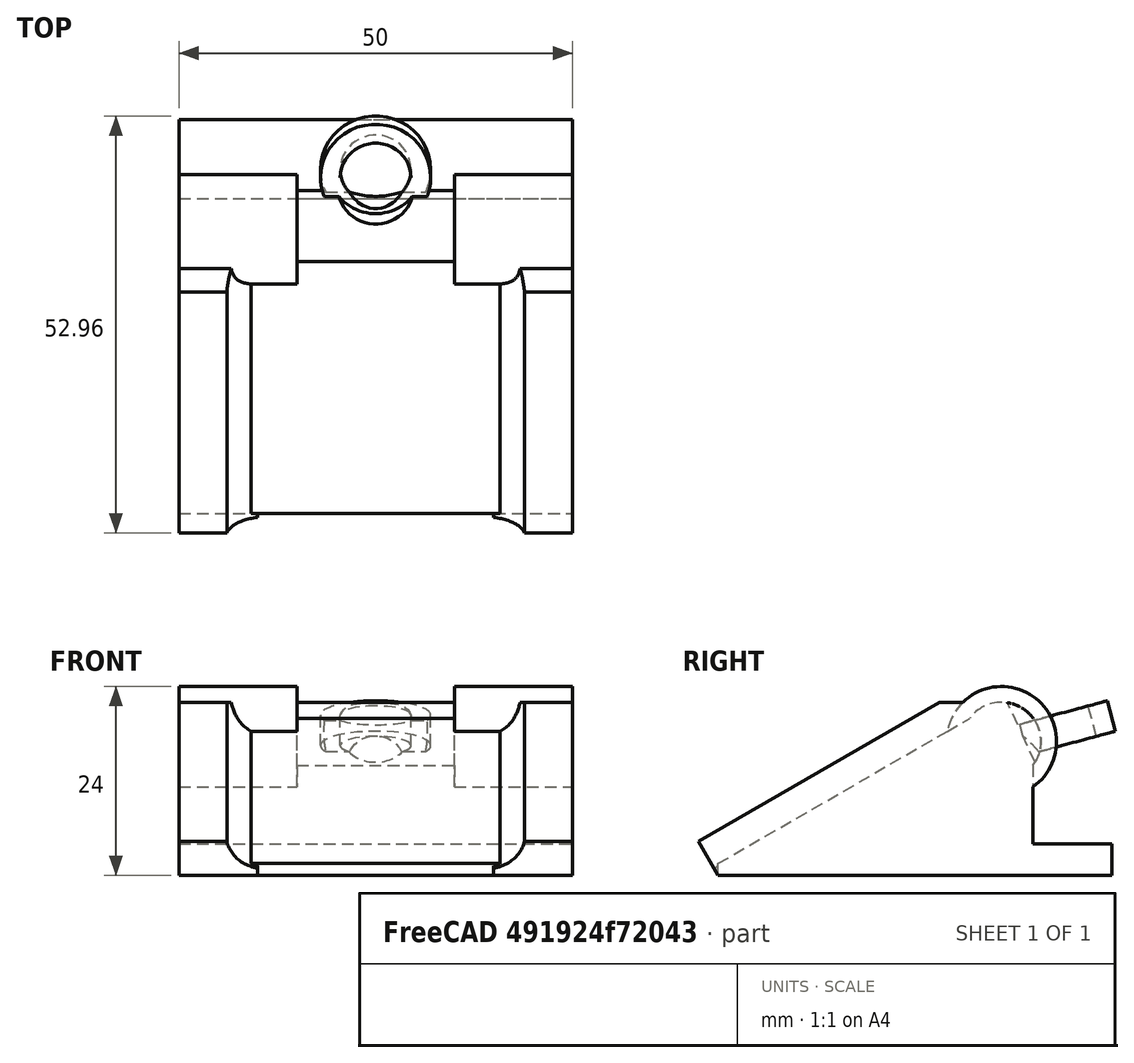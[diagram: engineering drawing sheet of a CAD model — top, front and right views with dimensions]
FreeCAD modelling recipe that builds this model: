
FCSTD DOCUMENT  (FreeCAD 0.18R16093 +53 (Git))
Label: mouse_surgery_bed
License: All rights reserved
LicenseURL: http://en.wikipedia.org/wiki/All_rights_reserved
objects: Part::Cylinder×8, Part::Box×7, Part::Cut×7, Part::MultiFuse×3
note: 25 computed .brp shape members not serialized (recipe doc carries the construction recipe); baked Part::Feature solids carry a one-line shape summary decoded from their .brp

FEATURE [Part::Box] Box  label="Cube"
  AttacherType = Attacher::AttachEngine3D
  Height = 20
  Length = 50
  Width = 40
FEATURE [Part::Cylinder] Cylinder
  Angle = 360
  AttacherType = Attacher::AttachEngine3D
  Height = 50
  Placement = pos=(0,36,17) rot=(0,1,0;1.5708rad)
  Radius = 5
FEATURE [Part::Box] Box001  label="Cube001"
  AttacherType = Attacher::AttachEngine3D
  Height = 17
  Length = 50
  Placement = pos=(0,0,1.5) rot=(1,0,0;0.523599rad)
  Width = 40
FEATURE [Part::Cut] Cut
  Base = -> Box
  Tool = -> Box001
FEATURE [Part::Box] Box002  label="Cube002"
  AttacherType = Attacher::AttachEngine3D
  Height = 5
  Length = 10
  Placement = pos=(0,0,0) rot=(1,0,0;0.523599rad)
  Width = 40
FEATURE [Part::Box] Box003  label="Cube003"
  AttacherType = Attacher::AttachEngine3D
  Height = 5
  Length = 10
  Placement = pos=(40,0,0) rot=(1,0,0;0.523599rad)
  Width = 40
FEATURE [Part::Cylinder] Cylinder001
  Angle = 360
  AttacherType = Attacher::AttachEngine3D
  Height = 45
  Placement = pos=(11,-5,4) rot=(-1,0,0;1.0472rad)
  Radius = 5
FEATURE [Part::Cylinder] Cylinder002
  Angle = 360
  AttacherType = Attacher::AttachEngine3D
  Height = 45
  Placement = pos=(39,-5,4) rot=(-1,0,0;1.0472rad)
  Radius = 5
FEATURE [Part::Cut] Cut001
  Base = -> Box002
  Tool = -> Cylinder001
FEATURE [Part::Cut] Cut002
  Base = -> Box003
  Tool = -> Cylinder002
FEATURE [Part::Box] Box004  label="Cube004"
  AttacherType = Attacher::AttachEngine3D
  Height = 10
  Length = 10
  Placement = pos=(0,27,22) rot=(0,0,1;0rad)
  Width = 10
FEATURE [Part::Box] Box005  label="Cube005"
  AttacherType = Attacher::AttachEngine3D
  Height = 10
  Length = 10
  Placement = pos=(40,27,22) rot=(0,0,1;0rad)
  Width = 10
FEATURE [Part::Cut] Cut003
  Base = -> Cut001
  Tool = -> Box004
FEATURE [Part::Cut] Cut004
  Base = -> Cut002
  Tool = -> Box005
FEATURE [Part::Cylinder] Cylinder003
  Angle = 360
  AttacherType = Attacher::AttachEngine3D
  Height = 20
  Placement = pos=(25,48,12) rot=(1,0,0;0.436332rad)
  Radius = 6
FEATURE [Part::MultiFuse] Fusion
  Shapes = -> [Cut,Cylinder]
FEATURE [Part::Cut] Cut005
  Base = -> Fusion
  Tool = -> Cylinder003
FEATURE [Part::MultiFuse] Fusion001
  Shapes = -> [Cut003,Cut004,Cut005]
FEATURE [Part::Cylinder] Cylinder004
  Angle = 360
  AttacherType = Attacher::AttachEngine3D
  Height = 15
  Placement = pos=(0,36,17) rot=(0,1,0;1.5708rad)
  Radius = 7
FEATURE [Part::Cylinder] Cylinder005
  Angle = 360
  AttacherType = Attacher::AttachEngine3D
  Height = 15
  Placement = pos=(35,36,17) rot=(0,1,0;1.5708rad)
  Radius = 7
FEATURE [Part::Cylinder] Cylinder006
  Angle = 360
  AttacherType = Attacher::AttachEngine3D
  Height = 4
  Placement = pos=(25,43.7,16.5) rot=(1,0,0;0.261799rad)
  Radius = 7
FEATURE [Part::Cylinder] Cylinder007
  Angle = 360
  AttacherType = Attacher::AttachEngine3D
  Height = 4
  Placement = pos=(25,43.7,16.5) rot=(1,0,0;0.261799rad)
  Radius = 4.5
FEATURE [Part::Cut] Cut006
  Base = -> Cylinder006
  Tool = -> Cylinder007
FEATURE [Part::Box] Box006  label="Cube006"
  AttacherType = Attacher::AttachEngine3D
  Height = 4
  Length = 50
  Placement = pos=(0,40,0) rot=(0,0,1;0rad)
  Width = 10
FEATURE [Part::MultiFuse] Fusion002
  Shapes = -> [Fusion001,Cylinder004,Cylinder005,Box006,Cut006]
